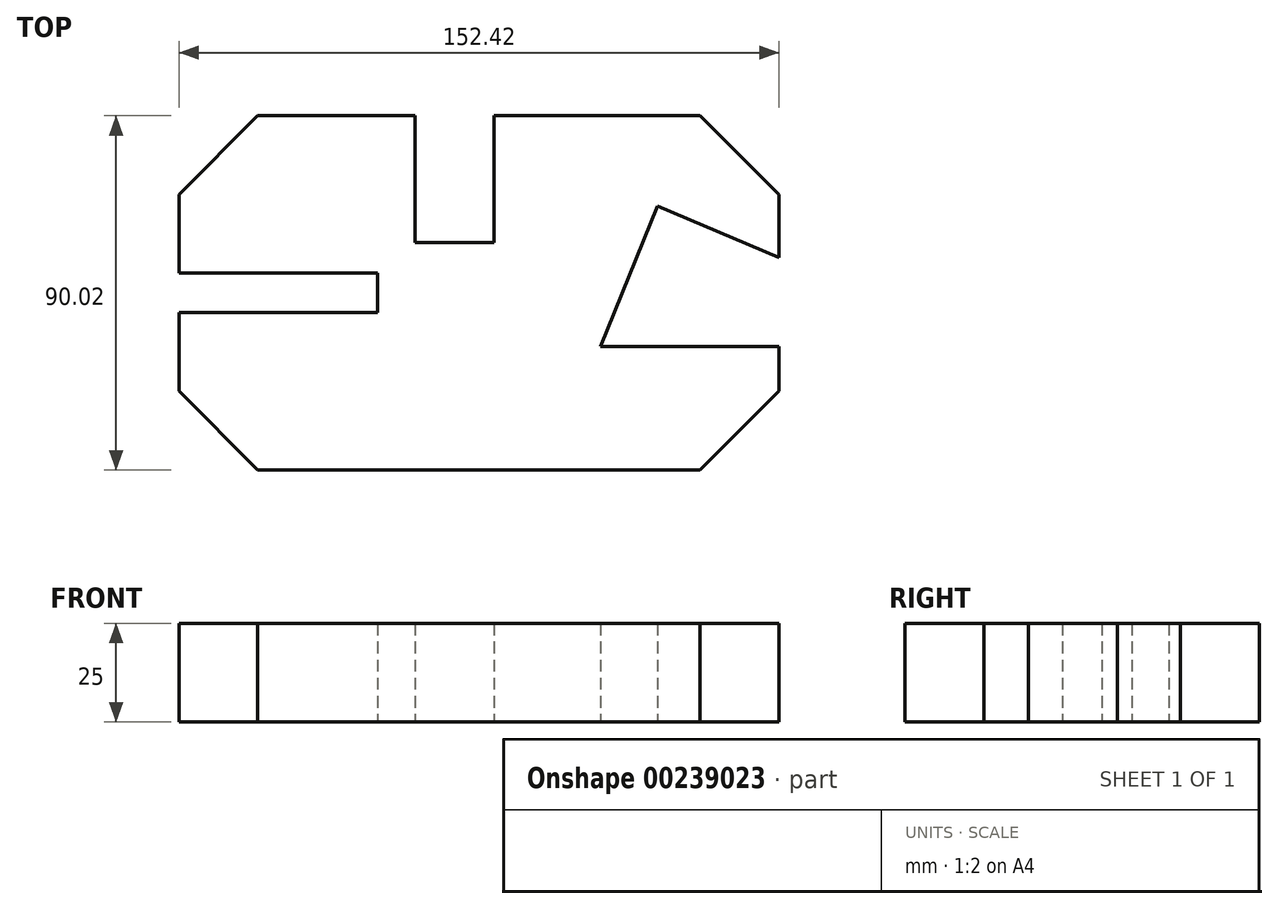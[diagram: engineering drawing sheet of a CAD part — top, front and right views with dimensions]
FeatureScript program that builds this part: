
annotation { "Feature Type Name" : "Feature", "Feature Type Description" : "" }
export const myFeature = defineFeature(function(context is Context, id is Id, definition is map)
    precondition{}
    {
        {
            var Q0;
            Q0=qCreatedBy(makeId("Top.planeOp"),FACE);
            var sketch = newSketch(context, id + "F0", { "sketchPlane" : qUnion([Q0])});
            skLineSegment(sketch, "E0", {"start": v(-53.08, -59.13) * mm, "end": v(59.32, -59.13) * mm});
            skLineSegment(sketch, "E1", {"start": v(59.32, -59.13) * mm, "end": v(79.3, -39.1) * mm});
            skLineSegment(sketch, "E2", {"start": v(-53.08, -59.13) * mm, "end": v(-73.1, -39.12) * mm});
            skPoint(sketch, "E3.orphan", {"position": v(-72.42, -59.13) * mm});
            skLineSegment(sketch, "E4", {"start": v(-53.08, -59.13) * mm, "end": v(-72.42, -59.13) * mm, "construction": true});
            skLineSegment(sketch, "E5", {"start": v(59.32, -59.13) * mm, "end": v(73.82, -59.11) * mm, "construction": true});
            skLineSegment(sketch, "E6", {"start": v(-73.1, -39.12) * mm, "end": v(-73.1, -19.12) * mm});
            skLineSegment(sketch, "E7", {"start": v(-73.1, -19.12) * mm, "end": v(-22.6, -19.12) * mm});
            skLineSegment(sketch, "E8", {"start": v(-22.6, -19.12) * mm, "end": v(-22.6, -9.12) * mm});
            skLineSegment(sketch, "E9", {"start": v(-22.6, -9.12) * mm, "end": v(-73.1, -9.12) * mm});
            skLineSegment(sketch, "E10", {"start": v(-73.1, -9.12) * mm, "end": v(-73.1, 10.88) * mm});
            skLineSegment(sketch, "E11", {"start": v(-73.1, 10.88) * mm, "end": v(-53.08, 30.9) * mm});
            skPoint(sketch, "E12.orphan", {"position": v(-72.42, 28.7) * mm});
            skLineSegment(sketch, "E13", {"start": v(-53.08, 30.9) * mm, "end": v(-13.08, 30.9) * mm});
            skLineSegment(sketch, "E14", {"start": v(-13.08, 30.9) * mm, "end": v(-13.08, -1.4) * mm});
            skLineSegment(sketch, "E15", {"start": v(-13.08, -1.4) * mm, "end": v(6.92, -1.4) * mm});
            skLineSegment(sketch, "E16", {"start": v(6.92, -1.4) * mm, "end": v(6.92, 30.87) * mm});
            skLineSegment(sketch, "E17", {"start": v(6.92, 30.87) * mm, "end": v(59.32, 30.87) * mm});
            skLineSegment(sketch, "E18", {"start": v(59.32, 30.87) * mm, "end": v(79.33, 10.86) * mm});
            skLineSegment(sketch, "E19", {"start": v(59.32, 30.87) * mm, "end": v(97.73, 30.87) * mm, "construction": true});
            skLineSegment(sketch, "E20", {"start": v(79.33, 10.86) * mm, "end": v(79.33, -5.14) * mm});
            skLineSegment(sketch, "E21", {"start": v(34.03, -27.73) * mm, "end": v(79.33, -27.73) * mm});
            skLineSegment(sketch, "E22", {"start": v(79.33, -27.73) * mm, "end": v(79.3, -39.1) * mm});
            skLineSegment(sketch, "E23", {"start": v(34.03, -27.73) * mm, "end": v(48.45, 7.97) * mm});
            skLineSegment(sketch, "E24", {"start": v(48.45, 7.97) * mm, "end": v(79.33, -5.14) * mm});
            skSolve(sketch);
        }
        {
            var Q0;
            Q0 = qSketchRegion(id + "F0", true);
            extrude(context, id + "F1", {"entities" : qUnion([Q0]), "depth" : 25 * mm});
        }
    });
